# Revit family: Sanitary_Basins_AXOR_38120XXX-AXOR-Uno-Electronic-basin-mixer_
name_source: partatom
category: Plumbing Fixtures
revit_build: Autodesk Revit 2018 (Build: 20170223_1515(x64)
units: mm (PartAtom-declared; Revit-internal decimal feet)

## family parameters
Always vertical = No
Cut with Voids When Loaded = No
OmniClass Number = 23.45.00.00
OmniClass Title = Sanitary, Laundry, and Cleaning Equipment
Part Type = Normal
Room Calculation Point = No
Round Connector Dimension = Use Diameter
Shared = No
Work Plane-Based = Yes

## types (1)
- Default - please load Revit Family Type Catalog
    Always visible = Yes
    BIMobject category = Basins
    Default Elevation = 1219.2 mm  [stored 4 ft]
    Design country = Germany
    EAN code = 4011097677880
    Edition number = 1
    GTIN code = https://4011097677880
    IFC Classification = Sanitary Terminal
    Installation instructions = https://www.axor-design.com
    Manufacturer country = Germany
    Manufacturer name = AXOR
    Material 1 = AXOR - AXOR One - 000 Chrome
    Material main = Chrome
    Product Guid = eb9d7781-fb7f-4c11-b3f1-6eac0b956c4f
    Product SKU = 38120XXX
    Product data url = https://www.bimobject.com
    Product family = AXOR Uno
    Product group = Electronic mixers
    Product name = 38120XXX AXOR Uno Electronic basin mixer for concealed installation wall-mounted with spout 225 mm
    Product url = https://www.axor-design.com
    QR code = https://www.bimobject.com
    Technical description = https://www.axor-design.com

note: [stored X ft] marks values corroborated as IEEE doubles in the binary element streams (Revit-internal decimal feet)

## geometry (parser evidence)
native form markers: Sweep x1
no freeform markers — native parametric forms only
